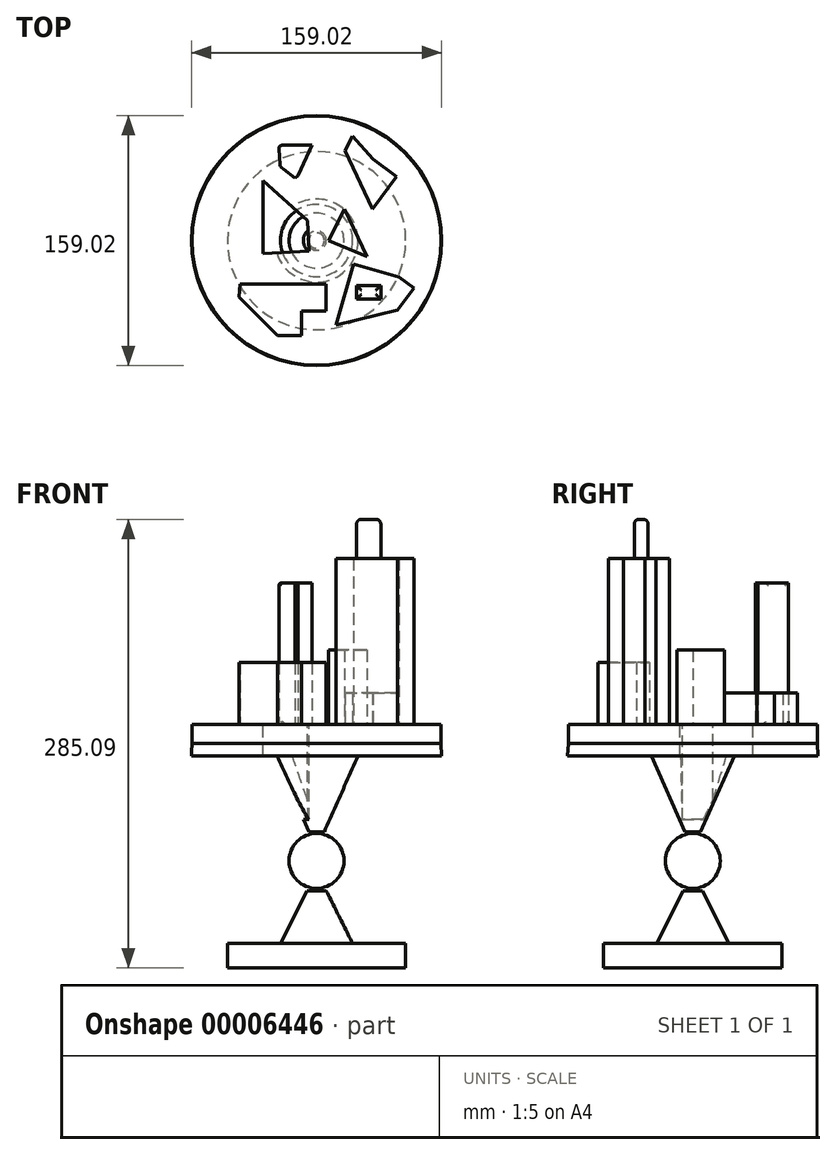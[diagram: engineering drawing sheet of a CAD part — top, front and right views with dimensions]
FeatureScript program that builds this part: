
annotation { "Feature Type Name" : "Feature", "Feature Type Description" : "" }
export const myFeature = defineFeature(function(context is Context, id is Id, definition is map)
    precondition{}
    {
        {
            var Q0;
            Q0=qCreatedBy(makeId("Front.planeOp"),FACE);
            var sketch = newSketch(context, id + "F0", { "sketchPlane" : qUnion([Q0])});
            skLineSegment(sketch, "E0", {"start": v(56.64, 0) * mm, "end": v(56.64, 15.6) * mm});
            skLineSegment(sketch, "E1", {"start": v(56.64, 15.6) * mm, "end": v(22.93, 15.6) * mm});
            skLineSegment(sketch, "E2", {"start": v(22.93, 15.6) * mm, "end": v(6.16, 49.18) * mm});
            skLineSegment(sketch, "E3", {"start": v(0, 49.18) * mm, "end": v(0, 0) * mm});
            skLineSegment(sketch, "E4", {"start": v(0, 0) * mm, "end": v(56.64, 0) * mm});
            skLineSegment(sketch, "E5", {"start": v(6.16, 49.18) * mm, "end": v(0, 49.18) * mm});
            skPoint(sketch, "E6.orphan", {"position": v(0, 61.5) * mm});
            skSolve(sketch);
        }
        {
            var Q0;
            Q0=makeQuery(id+"F0.imprint","IMPRINT",FACE,{"disambiguationData":[TD([[makeQuery(id+"F0.imprint","IMPRINT",EDGE,{"derivedFrom":sQuery(id+"F0.wireOp",EDGE,"E0")}),1.0]])]});
            var Q1;
            Q1=sQuery(id+"F0.wireOp",EDGE,"E3");
            revolve(context, id + "F1", {"entities" : qUnion([Q0]), "axis" : qUnion([Q1]), "revolveType" : RevolveType.FULL});
        }
        {
            var Q0;
            Q0=qCreatedBy(makeId("Front.planeOp"),FACE);
            var sketch = newSketch(context, id + "F2", { "sketchPlane" : qUnion([Q0])});
            skArc(sketch, "E7", {"start": v(0, 50.64) * mm, "mid": v(17.44, 68.07) * mm, "end": v(0, 85.51) * mm});
            skPoint(sketch, "E8.center.orphan", {"position": v(0, 87.28) * mm});
            skLineSegment(sketch, "E9", {"start": v(0, 50.64) * mm, "end": v(0, 85.51) * mm});
            skSolve(sketch);
        }
        {
            var Q0;
            Q0=makeQuery(id+"F2.imprint","IMPRINT",FACE,{"disambiguationData":[TD([[makeQuery(id+"F2.imprint","IMPRINT",EDGE,{"derivedFrom":sQuery(id+"F2.wireOp",EDGE,"E7")}),1.0]])]});
            var Q1;
            Q1=sQuery(id+"F2.wireOp",EDGE,"E9");
            revolve(context, id + "F3", {"entities" : qUnion([Q0]), "axis" : qUnion([Q1]), "revolveType" : RevolveType.FULL});
        }
        {
            var Q0;
            Q0=qCreatedBy(makeId("Right.planeOp"),FACE);
            var sketch = newSketch(context, id + "F4", { "sketchPlane" : qUnion([Q0])});
            skLineSegment(sketch, "E10", {"start": v(0, 85.54) * mm, "end": v(0, 142.73) * mm});
            skLineSegment(sketch, "E11", {"start": v(0, 142.73) * mm, "end": v(79.08, 142.73) * mm});
            skLineSegment(sketch, "E12", {"start": v(79.08, 142.73) * mm, "end": v(79.5, 134.8) * mm});
            skLineSegment(sketch, "E13", {"start": v(79.5, 134.8) * mm, "end": v(26.4, 135.07) * mm});
            skLineSegment(sketch, "E14", {"start": v(26.4, 135.07) * mm, "end": v(4.9, 86.5) * mm});
            skLineSegment(sketch, "E15", {"start": v(4.9, 86.5) * mm, "end": v(-0.13, 85.55) * mm});
            skSolve(sketch);
        }
        {
            var Q0;
            {var subQ4=sQuery(id+"F4.wireOp",EDGE,"E11");Q0=makeQuery(id+"F4.imprint","IMPRINT",FACE,{"disambiguationData":[TD([[makeQuery(id+"F4.imprint","IMPRINT",EDGE,{"derivedFrom":subQ4}),-1.0]])]});}
            var Q1;
            Q1=sQuery(id+"F4.wireOp",EDGE,"E10");
            revolve(context, id + "F5", {"entities" : qUnion([Q0]), "axis" : qUnion([Q1]), "revolveType" : RevolveType.FULL});
        }
        {
            var Q0;
            Q0=makeQuery(id+"F5.opRevolve","SWEPT_FACE",FACE,{"disambiguationData":[OSD([sQuery(id+"F4.wireOp",EDGE,"E11")])]});
            var sketch = newSketch(context, id + "F6", { "sketchPlane" : qUnion([Q0])});
            skLineSegment(sketch, "E16", {"start": v(-33.9, 38.03) * mm, "end": v(-33.9, -8.24) * mm});
            skLineSegment(sketch, "E17", {"start": v(-33.9, -8.24) * mm, "end": v(-4.67, -6.77) * mm});
            skLineSegment(sketch, "E18", {"start": v(-4.67, -6.77) * mm, "end": v(-5.65, 12.63) * mm});
            skLineSegment(sketch, "E19", {"start": v(-5.65, 12.63) * mm, "end": v(-33.9, 38.03) * mm});
            skSolve(sketch);
        }
        {
            var Q0;
            Q0=makeQuery(id+"F6.imprint","IMPRINT",FACE,{"disambiguationData":[TD([[makeQuery(id+"F6.imprint","IMPRINT",EDGE,{"derivedFrom":sQuery(id+"F6.wireOp",EDGE,"E16")}),1.0]])]});
            extrude(context, id + "F7", {"entities" : qUnion([Q0]), "operationType" : NewBodyOperationType.REMOVE, "oppositeDirection" : true, "depth" : 48.35 * mm});
        }
        {
            var Q0;
            Q0=makeQuery(id+"F5.opRevolve","SWEPT_FACE",FACE,{"disambiguationData":[OSD([sQuery(id+"F4.wireOp",EDGE,"E11")])]});
            var sketch = newSketch(context, id + "F8", { "sketchPlane" : qUnion([Q0])});
            skLineSegment(sketch, "E20", {"start": v(17.8, 20) * mm, "end": v(7.57, 0) * mm});
            skLineSegment(sketch, "E21", {"start": v(7.57, 0) * mm, "end": v(32.06, -10.2) * mm});
            skLineSegment(sketch, "E22", {"start": v(32.06, -10.2) * mm, "end": v(17.8, 20) * mm});
            skSolve(sketch);
        }
        {
            var Q0;
            Q0=makeQuery(id+"F8.imprint","IMPRINT",FACE,{"disambiguationData":[TD([[makeQuery(id+"F8.imprint","IMPRINT",EDGE,{"derivedFrom":sQuery(id+"F8.wireOp",EDGE,"E20")}),1.0]])]});
            extrude(context, id + "F9", {"entities" : qUnion([Q0]), "operationType" : NewBodyOperationType.ADD, "depth" : 59.23 * mm});
        }
        {
            var Q0;
            Q0=makeQuery(id+"F5.opRevolve","SWEPT_FACE",FACE,{"disambiguationData":[OSD([sQuery(id+"F4.wireOp",EDGE,"E11")])]});
            var sketch = newSketch(context, id + "F10", { "sketchPlane" : qUnion([Q0])});
            skLineSegment(sketch, "E23.bottom", {"start": v(-9.68, -42.32) * mm, "end": v(40.32, -42.32) * mm});
            skLineSegment(sketch, "E23.top", {"start": v(-9.68, -32.32) * mm, "end": v(40.32, -32.32) * mm});
            skLineSegment(sketch, "E23.left", {"start": v(-9.68, -42.32) * mm, "end": v(-9.68, -32.32) * mm});
            skLineSegment(sketch, "E23.right", {"start": v(40.32, -42.32) * mm, "end": v(40.32, -32.32) * mm});
            skSolve(sketch);
        }
        {
            var Q0;
            Q0=makeQuery(id+"F10.imprint","IMPRINT",FACE,{"disambiguationData":[TD([[makeQuery(id+"F10.imprint","IMPRINT",EDGE,{"derivedFrom":sQuery(id+"F10.wireOp",EDGE,"E23.bottom")}),1.0]])]});
            var Q1;
            Q1=makeQuery(id+"F10.imprint","IMPRINT",FACE,{"disambiguationData":[TD([[makeQuery(id+"F10.imprint","IMPRINT",EDGE,{"derivedFrom":sQuery(id+"F10.wireOp",EDGE,"E23.bottom")}),-1.0]])]});
            extrude(context, id + "F11", {"entities" : qUnion([Q0, Q1]), "operationType" : NewBodyOperationType.ADD, "depth" : 12 * mm});
        }
        {
            var Q0;
            Q0=makeQuery(id+"F11.opExtrude","CAP_FACE",FACE,{"disambiguationData":[OSD([sQuery(id+"F4.wireOp",EDGE,"E11"),sQuery(id+"F4.wireOp",EDGE,"E12"),sQuery(id+"F6.wireOp",EDGE,"E16"),sQuery(id+"F6.wireOp",EDGE,"E17"),sQuery(id+"F6.wireOp",EDGE,"E18"),sQuery(id+"F6.wireOp",EDGE,"E19"),sQuery(id+"F8.wireOp",EDGE,"E20"),sQuery(id+"F8.wireOp",EDGE,"E21"),sQuery(id+"F8.wireOp",EDGE,"E22")])],"isStart":false});
            var sketch = newSketch(context, id + "F12", { "sketchPlane" : qUnion([Q0])});
            skLineSegment(sketch, "E24", {"start": v(-49.14, -35.94) * mm, "end": v(-24.92, -60.16) * mm});
            skLineSegment(sketch, "E25", {"start": v(-24.92, -60.16) * mm, "end": v(-9.4, -60.16) * mm});
            skLineSegment(sketch, "E26", {"start": v(-9.4, -60.16) * mm, "end": v(-9.4, -44.63) * mm});
            skLineSegment(sketch, "E27", {"start": v(-9.4, -44.63) * mm, "end": v(6.13, -44.63) * mm});
            skLineSegment(sketch, "E28", {"start": v(6.13, -44.63) * mm, "end": v(6.13, -27.7) * mm});
            skLineSegment(sketch, "E29", {"start": v(6.13, -27.7) * mm, "end": v(-48.66, -27.7) * mm});
            skLineSegment(sketch, "E30", {"start": v(-48.66, -27.7) * mm, "end": v(-49.14, -35.94) * mm});
            skSolve(sketch);
        }
        {
            var Q0;
            Q0=makeQuery(id+"F12.imprint","IMPRINT",FACE,{"disambiguationData":[TD([[makeQuery(id+"F12.imprint","IMPRINT",EDGE,{"derivedFrom":sQuery(id+"F12.wireOp",EDGE,"E24")}),1.0]])]});
            extrude(context, id + "F13", {"entities" : qUnion([Q0]), "operationType" : NewBodyOperationType.ADD, "depth" : 39.44 * mm});
        }
        {
            var Q0;
            Q0=makeQuery(id+"F11.opExtrude","CAP_FACE",FACE,{"disambiguationData":[OSD([sQuery(id+"F4.wireOp",EDGE,"E11"),sQuery(id+"F4.wireOp",EDGE,"E12"),sQuery(id+"F6.wireOp",EDGE,"E16"),sQuery(id+"F6.wireOp",EDGE,"E17"),sQuery(id+"F6.wireOp",EDGE,"E18"),sQuery(id+"F6.wireOp",EDGE,"E19"),sQuery(id+"F8.wireOp",EDGE,"E20"),sQuery(id+"F8.wireOp",EDGE,"E21"),sQuery(id+"F8.wireOp",EDGE,"E22")])],"isStart":false});
            var sketch = newSketch(context, id + "F14", { "sketchPlane" : qUnion([Q0])});
            skLineSegment(sketch, "E31", {"start": v(18.09, 57.04) * mm, "end": v(35.6, 20) * mm});
            skLineSegment(sketch, "E32", {"start": v(35.6, 20) * mm, "end": v(50.8, 40.8) * mm});
            skLineSegment(sketch, "E33", {"start": v(50.8, 40.8) * mm, "end": v(35.9, 51.7) * mm});
            skLineSegment(sketch, "E34", {"start": v(35.9, 51.7) * mm, "end": v(22.74, 66.28) * mm});
            skLineSegment(sketch, "E35", {"start": v(22.74, 66.28) * mm, "end": v(18.09, 57.04) * mm});
            skSolve(sketch);
        }
        {
            var Q0;
            Q0=makeQuery(id+"F14.imprint","IMPRINT",FACE,{"disambiguationData":[TD([[makeQuery(id+"F14.imprint","IMPRINT",EDGE,{"derivedFrom":sQuery(id+"F14.wireOp",EDGE,"E31")}),1.0]])]});
            var sketch = newSketch(context, id + "F15", { "sketchPlane" : qUnion([Q0])});
            skSolve(sketch);
        }
        {
            var Q0;
            Q0=makeQuery(id+"F15.imprint","IMPRINT",FACE,{"disambiguationData":[TD([[makeQuery(id+"F15.imprint","IMPRINT",EDGE,{"derivedFrom":makeQuery(id+"F14.imprint","IMPRINT",EDGE,{"derivedFrom":sQuery(id+"F14.wireOp",EDGE,"E31")})}),1.0]])]});
            extrude(context, id + "F16", {"entities" : qUnion([Q0]), "operationType" : NewBodyOperationType.ADD, "depth" : 20 * mm});
        }
        {
            var Q0;
            Q0=makeQuery(id+"F14.imprint","IMPRINT",FACE,{"disambiguationData":[TD([[makeQuery(id+"F14.imprint","IMPRINT",EDGE,{"derivedFrom":sQuery(id+"F14.wireOp",EDGE,"E31")}),-1.0]])]});
            var sketch = newSketch(context, id + "F17", { "sketchPlane" : qUnion([Q0])});
            skLineSegment(sketch, "E36", {"start": v(12.5, -53.5) * mm, "end": v(23.52, -15.04) * mm});
            skLineSegment(sketch, "E37", {"start": v(23.52, -15.04) * mm, "end": v(52.36, -23.3) * mm});
            skLineSegment(sketch, "E38", {"start": v(52.36, -23.3) * mm, "end": v(61.98, -30.3) * mm});
            skLineSegment(sketch, "E39", {"start": v(61.98, -30.3) * mm, "end": v(51.46, -44.25) * mm});
            skLineSegment(sketch, "E40", {"start": v(51.46, -44.25) * mm, "end": v(12.5, -53.5) * mm});
            skSolve(sketch);
        }
        {
            var Q0;
            Q0=makeQuery(id+"F17.imprint","IMPRINT",FACE,{"disambiguationData":[TD([[makeQuery(id+"F17.imprint","IMPRINT",EDGE,{"derivedFrom":sQuery(id+"F17.wireOp",EDGE,"E36")}),-1.0]])]});
            extrude(context, id + "F18", {"entities" : qUnion([Q0]), "operationType" : NewBodyOperationType.ADD, "depth" : 105.36 * mm});
        }
        {
            var Q0;
            Q0=makeQuery(id+"F14.imprint","IMPRINT",FACE,{"disambiguationData":[TD([[makeQuery(id+"F14.imprint","IMPRINT",EDGE,{"derivedFrom":sQuery(id+"F14.wireOp",EDGE,"E31")}),-1.0]])]});
            var sketch = newSketch(context, id + "F19", { "sketchPlane" : qUnion([Q0])});
            skLineSegment(sketch, "E41", {"start": v(-24.05, 60.53) * mm, "end": v(-2.77, 60.53) * mm});
            skLineSegment(sketch, "E42", {"start": v(-2.77, 60.53) * mm, "end": v(-11.7, 41.42) * mm});
            skLineSegment(sketch, "E43", {"start": v(-11.7, 41.42) * mm, "end": v(-13.56, 39.7) * mm});
            skLineSegment(sketch, "E44", {"start": v(-13.56, 39.7) * mm, "end": v(-23.12, 47.04) * mm});
            skLineSegment(sketch, "E45", {"start": v(-23.12, 47.04) * mm, "end": v(-24.05, 60.53) * mm});
            skSolve(sketch);
        }
        {
            var Q0;
            Q0 = qSketchRegion(id + "F19", true);
            extrude(context, id + "F20", {"entities" : qUnion([Q0]), "operationType" : NewBodyOperationType.ADD, "depth" : 90 * mm});
        }
        {
            var Q0;
            Q0=makeQuery(id+"F20.opExtrude","CAP_EDGE",EDGE,{"disambiguationData":[OSD([sQuery(id+"F19.wireOp",EDGE,"E45")])],"isStart":true});
            var Q1;
            Q1=makeQuery(id+"F20.opExtrude","CAP_EDGE",EDGE,{"disambiguationData":[OSD([sQuery(id+"F19.wireOp",EDGE,"E42")])],"isStart":true});
            var Q2;
            Q2=makeQuery(id+"F20.opExtrude","CAP_EDGE",EDGE,{"disambiguationData":[OSD([sQuery(id+"F19.wireOp",EDGE,"E41")])],"isStart":true});
            var Q3;
            Q3=makeQuery(id+"F20.opExtrude","CAP_EDGE",EDGE,{"disambiguationData":[OSD([sQuery(id+"F19.wireOp",EDGE,"E44")])],"isStart":true});
            var Q4;
            Q4=makeQuery(id+"F20.opExtrude","CAP_EDGE",EDGE,{"disambiguationData":[OSD([sQuery(id+"F19.wireOp",EDGE,"E43")])],"isStart":true});
            var Q5;
            Q5=makeQuery(id+"F20.opExtrude","SWEPT_FACE",FACE,{"disambiguationData":[OSD([sQuery(id+"F19.wireOp",EDGE,"E45")])]});
            fillet(context, id + "F21", {"entities" : qUnion([Q0, Q1, Q2, Q3, Q4, Q5]), "radius" : 2 * mm, "tangentPropagation" : true, "allowEdgeOverflow" : false});
        }
        {
            var Q0;
            Q0=makeQuery(id+"F18.opExtrude","CAP_FACE",FACE,{"disambiguationData":[OSD([sQuery(id+"F17.wireOp",EDGE,"E36"),sQuery(id+"F17.wireOp",EDGE,"E37"),sQuery(id+"F17.wireOp",EDGE,"E38"),sQuery(id+"F17.wireOp",EDGE,"E39"),sQuery(id+"F17.wireOp",EDGE,"E40")])],"isStart":false});
            var sketch = newSketch(context, id + "F22", { "sketchPlane" : qUnion([Q0])});
            skLineSegment(sketch, "E46.bottom", {"start": v(25.44, -28.5) * mm, "end": v(40.8, -28.5) * mm});
            skLineSegment(sketch, "E46.top", {"start": v(25.44, -37.2) * mm, "end": v(40.8, -37.2) * mm});
            skLineSegment(sketch, "E46.left", {"start": v(25.44, -28.5) * mm, "end": v(25.44, -37.2) * mm});
            skLineSegment(sketch, "E46.right", {"start": v(40.8, -28.5) * mm, "end": v(40.8, -37.2) * mm});
            skSolve(sketch);
        }
        {
            var Q0;
            Q0=makeQuery(id+"F22.imprint","IMPRINT",FACE,{"disambiguationData":[TD([[makeQuery(id+"F22.imprint","IMPRINT",EDGE,{"derivedFrom":sQuery(id+"F22.wireOp",EDGE,"E46.bottom")}),-1.0]])]});
            extrude(context, id + "F23", {"entities" : qUnion([Q0]), "operationType" : NewBodyOperationType.ADD, "depth" : 25 * mm});
        }
        {
            var Q0;
            Q0=makeQuery(id+"F23.opExtrude","CAP_EDGE",EDGE,{"disambiguationData":[OSD([sQuery(id+"F22.wireOp",EDGE,"E46.top")])],"isStart":false});
            var Q1;
            Q1=makeQuery(id+"F23.opExtrude","CAP_EDGE",EDGE,{"disambiguationData":[OSD([sQuery(id+"F22.wireOp",EDGE,"E46.right")])],"isStart":false});
            var Q2;
            Q2=makeQuery(id+"F23.opExtrude","CAP_EDGE",EDGE,{"disambiguationData":[OSD([sQuery(id+"F22.wireOp",EDGE,"E46.left")])],"isStart":false});
            var Q3;
            Q3=makeQuery(id+"F23.opExtrude","CAP_EDGE",EDGE,{"disambiguationData":[OSD([sQuery(id+"F22.wireOp",EDGE,"E46.bottom")])],"isStart":false});
            fillet(context, id + "F24", {"entities" : qUnion([Q0, Q1, Q2, Q3]), "radius" : 3 * mm, "tangentPropagation" : true, "allowEdgeOverflow" : false});
        }
    });
